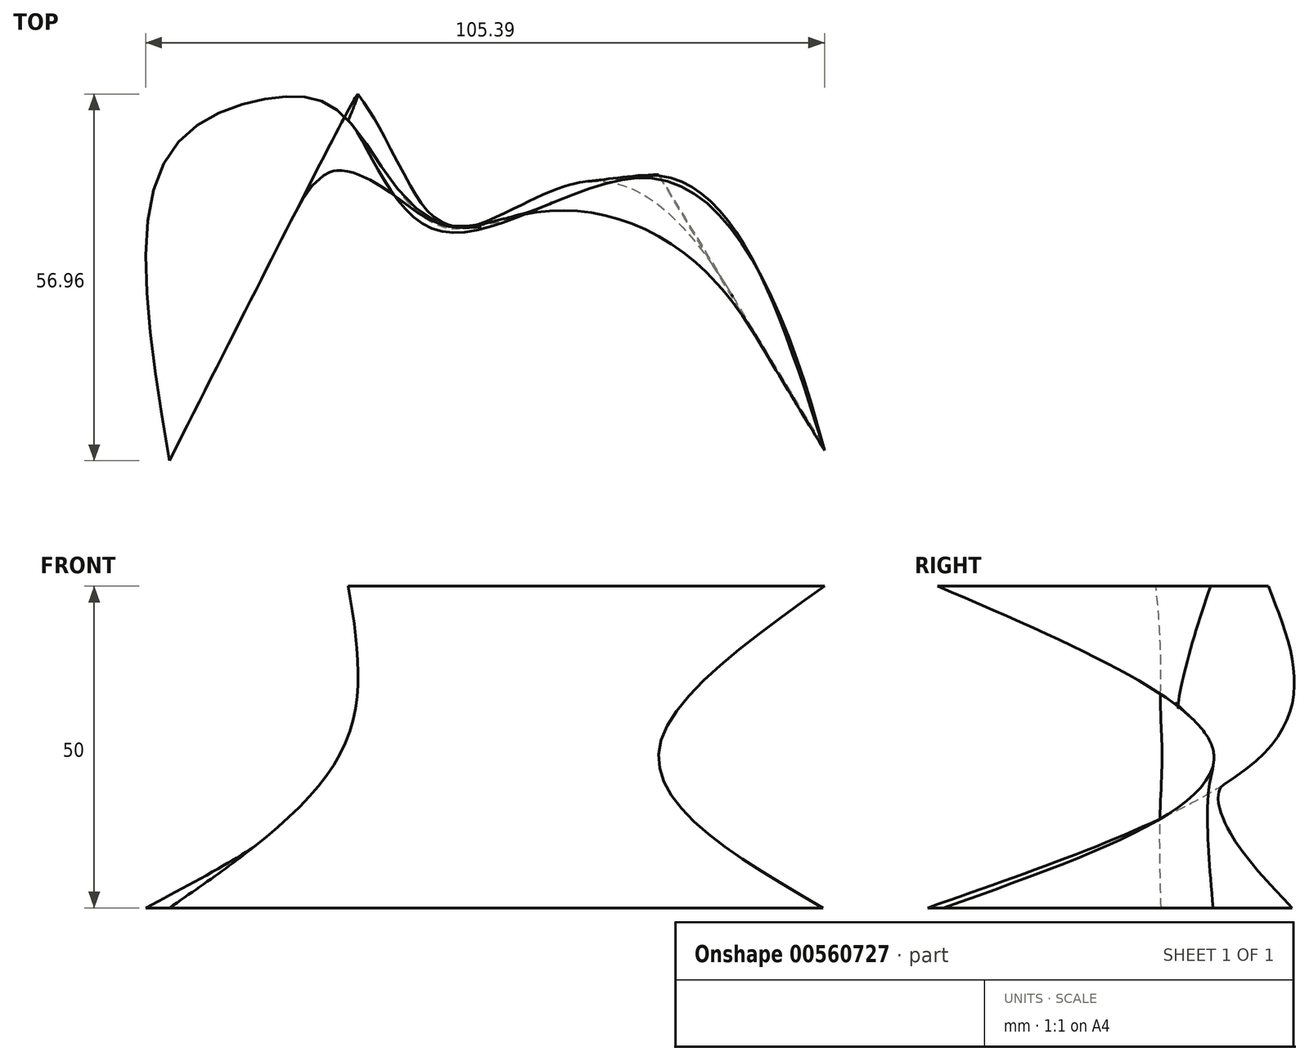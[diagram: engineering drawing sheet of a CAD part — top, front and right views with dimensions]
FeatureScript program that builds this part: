
annotation { "Feature Type Name" : "Feature", "Feature Type Description" : "" }
export const myFeature = defineFeature(function(context is Context, id is Id, definition is map)
    precondition{}
    {
        {
            var Q0;
            Q0=qCreatedBy(makeId("Top.planeOp"),FACE);
            var sketch = newSketch(context, id + "F0", { "sketchPlane" : qUnion([Q0])});
            skFitSpline(sketch, "E0", {"points": [v(-71.26, -14.98) * mm, v(-71.5, 32.37) * mm, v(-54.11, 41.55) * mm, v(-43.48, 37.93) * mm, v(-27.78, 21.5) * mm, v(5.31, 29.23) * mm, v(30.2, -12.56) * mm], "startDerivative": vector(-44.28, 264.8) * mm, "endDerivative": vector(88.93, -276.94) * mm});
            skSolve(sketch);
        }
        {
            var Q0;
            Q0=qCreatedBy(makeId("Top.planeOp"),FACE);
            cPlane(context, id + "F1", {"entities" : qUnion([Q0]), "cplaneType" : CPlaneType.OFFSET, "offset" : 25 * mm, "width" : 150 * mm, "height" : 150 * mm});
        }
        {
            var Q0;
            Q0=qCreatedBy(id+"F1.planeOp",FACE);
            var sketch = newSketch(context, id + "F2", { "sketchPlane" : qUnion([Q0])});
            skFitSpline(sketch, "E1", {"points": [v(-71.5, -15.22) * mm, v(-71.5, 32.37) * mm, v(-55.08, 41.8) * mm, v(-44.2, 38.17) * mm], "startDerivative": vector(-18.66, 119.1) * mm, "endDerivative": vector(28.2, -37.6) * mm});
            skFitSpline(sketch, "E2", {"points": [v(-44.2, 38.17) * mm, v(-28.99, 21.74) * mm, v(4.83, 29.23) * mm], "startDerivative": vector(43.9, -40.65) * mm, "endDerivative": vector(66.68, 3.92) * mm});
            skFitSpline(sketch, "E3", {"points": [v(4.83, 29.23) * mm, v(29.95, -12.08) * mm], "startDerivative": vector(55.08, -22.47) * mm, "endDerivative": vector(10.15, -36.23) * mm});
            skSolve(sketch);
        }
        {
            var Q0;
            Q0=qCreatedBy(id+"F1.planeOp",FACE);
            cPlane(context, id + "F3", {"entities" : qUnion([Q0]), "cplaneType" : CPlaneType.OFFSET, "offset" : 25 * mm, "width" : 150 * mm, "height" : 150 * mm});
        }
        {
            var Q0;
            Q0=qCreatedBy(id+"F3.planeOp",FACE);
            var sketch = newSketch(context, id + "F4", { "sketchPlane" : qUnion([Q0])});
            skFitSpline(sketch, "E4", {"points": [v(-71.99, -14.98) * mm, v(-71.26, 32.13) * mm, v(-55.56, 41.8) * mm, v(-43.48, 37.93) * mm], "startDerivative": vector(-15.76, 118.7) * mm, "endDerivative": vector(59.9, -44.93) * mm});
            skFitSpline(sketch, "E5", {"points": [v(-43.48, 37.93) * mm, v(-29.95, 20.91) * mm, v(3.87, 28.88) * mm, v(30.44, -13.4) * mm], "startDerivative": vector(32.87, -34.02) * mm, "endDerivative": vector(39.76, -151.85) * mm});
            skSolve(sketch);
        }
        {
            var Q0;
            Q0=sQuery(id+"F4.wireOp",EDGE,"E5");
            var Q1;
            Q1=sQuery(id+"F2.wireOp",EDGE,"E2");
            var Q2;
            Q2=sQuery(id+"F0.wireOp",EDGE,"E0");
            loft(context, id + "F5", {"bodyType" : ToolBodyType.SURFACE, "wireProfilesArray" : [{ "wireProfileEntities" : qUnion([Q0]) }, { "wireProfileEntities" : qUnion([Q1]) }, { "wireProfileEntities" : qUnion([Q2]) }]});
        }
    });
